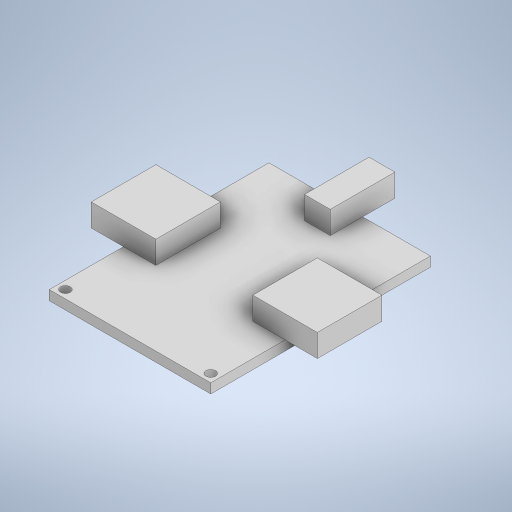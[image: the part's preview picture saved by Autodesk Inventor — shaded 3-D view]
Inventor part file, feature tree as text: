
AUTODESK INVENTOR PART (.ipt)
format: ipt  version: 2023 (Build 270158000, 158)  size: 303,104 bytes
history: native  units: in
note: dims shown in document units (in); Inventor stores cm internally (conversion verified against a paired STEP export)
features: extrude x5, sketch x5
ambient origin geometry x8: Origin, YZ Plane, XZ Plane, XY Plane, X Axis, Y Axis, Z Axis, Center Point
bodies: Solid1 (feature_tree)
feature tree (10):
  extrude  "Extrusion1"  Depth=1.7717in
  extrude  "Extrusion2"  Depth=0.1181in
  extrude  "Extrusion3"  Depth=0.1181in
  extrude  "Extrusion4"  Depth=2.6772in
  extrude  "Extrusion5"  Depth=0.3937in
  sketch  "Sketch1"  dims[d0=1.7717in d1=1.7717in]
  sketch  "Sketch2"  dims[d2=0.1181in d3=0.1181in]
  sketch  "Sketch3"  dims[d4=0.1181in d5=0.1181in]
  sketch  "Sketch4"  dims[d6=1.9685in d7=2.6772in]
  sketch  "Sketch5"  dims[d8=0.0984in d9=0.0984in d10=0.1181in d11=0.0in d12=0.3937in d13=0.7874in d14=0.9843in d15=0.3937in d16=0.7874in d17=0.2756in d18=0.0in d19=0.315in d20=0.3937in d21=1.9685in d22=2.6772in d23=0.8268in d24=0.3937in d25=0.0in d26=0.3937in d27=0.0in d28=0.3937in d29=0.0in]
